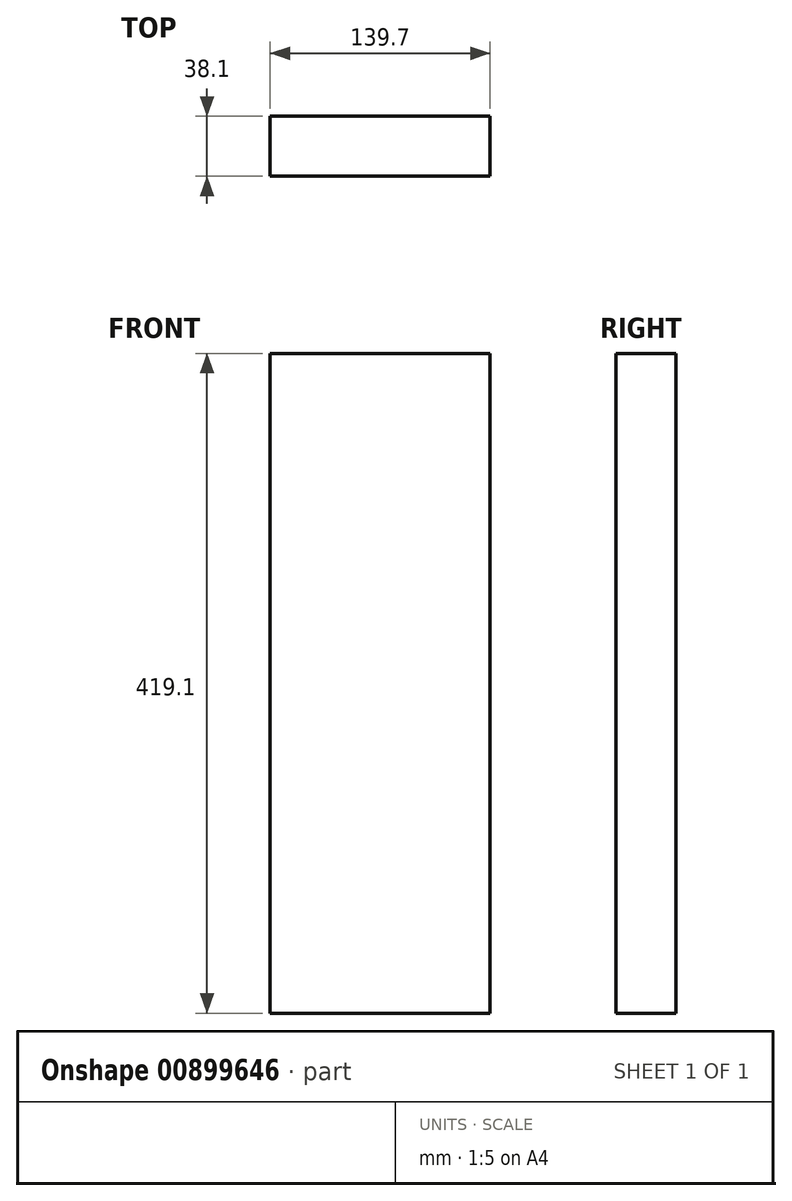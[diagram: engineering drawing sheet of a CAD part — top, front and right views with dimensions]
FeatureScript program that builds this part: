
annotation { "Feature Type Name" : "Feature", "Feature Type Description" : "" }
export const myFeature = defineFeature(function(context is Context, id is Id, definition is map)
    precondition{}
    {
        {
            var Q0;
            Q0=qCreatedBy(makeId("Front.planeOp"),FACE);
            var sketch = newSketch(context, id + "F0", { "sketchPlane" : qUnion([Q0])});
            skLineSegment(sketch, "E0.bottom", {"start": v(0, 0) * mm, "end": v(139.7, 0) * mm});
            skLineSegment(sketch, "E0.top", {"start": v(0, 419.1) * mm, "end": v(139.7, 419.1) * mm});
            skLineSegment(sketch, "E0.left", {"start": v(0, 0) * mm, "end": v(0, 419.1) * mm});
            skLineSegment(sketch, "E0.right", {"start": v(139.7, 0) * mm, "end": v(139.7, 419.1) * mm});
            skSolve(sketch);
        }
        {
            var Q0;
            Q0=makeQuery(id+"F0.imprint","IMPRINT",FACE,{"disambiguationData":[TD([[makeQuery(id+"F0.imprint","IMPRINT",EDGE,{"derivedFrom":sQuery(id+"F0.wireOp",EDGE,"E0.bottom")}),1.0]])]});
            extrude(context, id + "F1", {"entities" : qUnion([Q0]), "oppositeDirection" : true, "depth" : 38.1 * mm, "offsetDistance" : 25.4 * mm});
        }
    });
